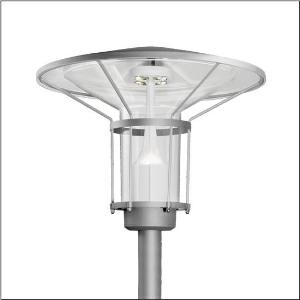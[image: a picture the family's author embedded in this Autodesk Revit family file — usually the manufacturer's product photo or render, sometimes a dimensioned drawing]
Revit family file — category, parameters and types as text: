
# Revit family: laterne_classic_iq___p1_0a_5xa5245nf14hp_be56
name_source: partatom
category: Lighting Fixtures
units: mm (PartAtom-declared; Revit-internal decimal feet)

## family parameters
Cut with Voids When Loaded = No
Host = Face
Light Source = No
Part Type = Normal
Room Calculation Point = No
Round Connector Dimension = Use Diameter
Shared = No

## types (1)
- --- (1 x LED, 3780 lm, 33.6 W, 2700K)
    Apparent Load = 34 VA
    CIE Flux Codes = 31 61 91 96 100
    Color Rendering = 70
    Color Temperature = 2700K
    Default Elevation = 1800 mm
    Description = Lantern Classic iQ, mast luminaire, Module 540 iQ-SR, primary light control with 3 zone facetted reflector, of plastic, silver coated, highly specular, structured, primary optical cover: cover, of PMMA, transparent, light distribution: P1.0a, light emission: direct distribution, primary light characteristic: strongly asymmetric, installation type: post-top, LED, High Power LED, rated luminous flux: 3.780lm, luminous efficacy: 113lm/W, light colour: 727, colour temperature: 2700K, control gear: ECG iQ, control: pre-setting: logarithmic dimming characteristic, Street-Remote, Auto-Match, Temp-Guard, Lumen-Switch, Night-Set, Smart-Wire, Light-Fading, Desk-Remote (wireless, voltage-free reading and setting of iQ features in the workshop via application-optimized NFC function/RFID function), optimised constant luminous flux control (CLO 2.0), with terminal, 6-pole, max. 2.5mm², mains connection: 230..240V, AC, 50/60Hz, start of lifetime: 34W, end of service life: 36W, reduction: 15W, luminaire housing, upper part, of glass-fibre reinforced polyester, coated, Siteco® metallic grey (DB 702S), diameter: 750mm, height: 596mm, spigot size: d x l = 76 x 70mm (post-top) | with reducer (optional accessory) 60 x 70mm, post-top mast mounting element, of diecast aluminium, coated, Siteco® metallic grey (DB 702S), Module 540 iQ-SR, traffic white (RAL 9016), equipment: Power, protection rating (complete): IP65, insulation class (complete): insulation class II (safety insulation), certification: CE, ENEC, VDE, packaging unit: 1 piece

Light Distribution: P1.0a
    Height = 596 mm
    Lamp = 1 x LED
    Lamp Light Flux = 3780 lm
    Lamp Power = 33.6 W
    Lamp count = 1
    Length = 750 mm
    Luminous efficacy = 113 lm/W
    Manufacturer = Siteco
    ModVariant = No
    Model = 5XA5245NF14HP
    Number of Poles = 1
    OnlyDefault = Yes
    Power Factor = 1
    Product Name = Laterne Classic iQ | P1.0a
    Product group = mast luminaire | pylon top
    ProductGroupID = 6100
    Protection Class = Protection class II
    Protection Degree = IP 65
    RLX_Detail_Level = 1
    RLX_Emergency_Light_Flux = 0 lm
    RLX_Emergency_Type = 0
    RLX_Emergency_Type_DB = No
    RlxData = <blob elided: 65529 chars, md5=52ee965f>
    Socket = socket
    Standby Power = 0 W
    System Light Flux = 3780 lm
    System Power = 34 W
    Type Comments = factory setting: luminous flux: 100 % | dim-lin: 254 | 695 mA
    Type Image = l_1006052.jpg
    URL = http://relux.com
    VarID = @adj_122989
    Voltage = 0 V
    Weight = 0.00 kg
    Width = 0 mm  [stored 0 ft]

note: [stored X ft] marks values corroborated as IEEE doubles in the binary element streams (Revit-internal decimal feet)

## geometry (parser evidence)
native form markers: Blend x4, Sweep x10
no freeform markers — native parametric forms only
